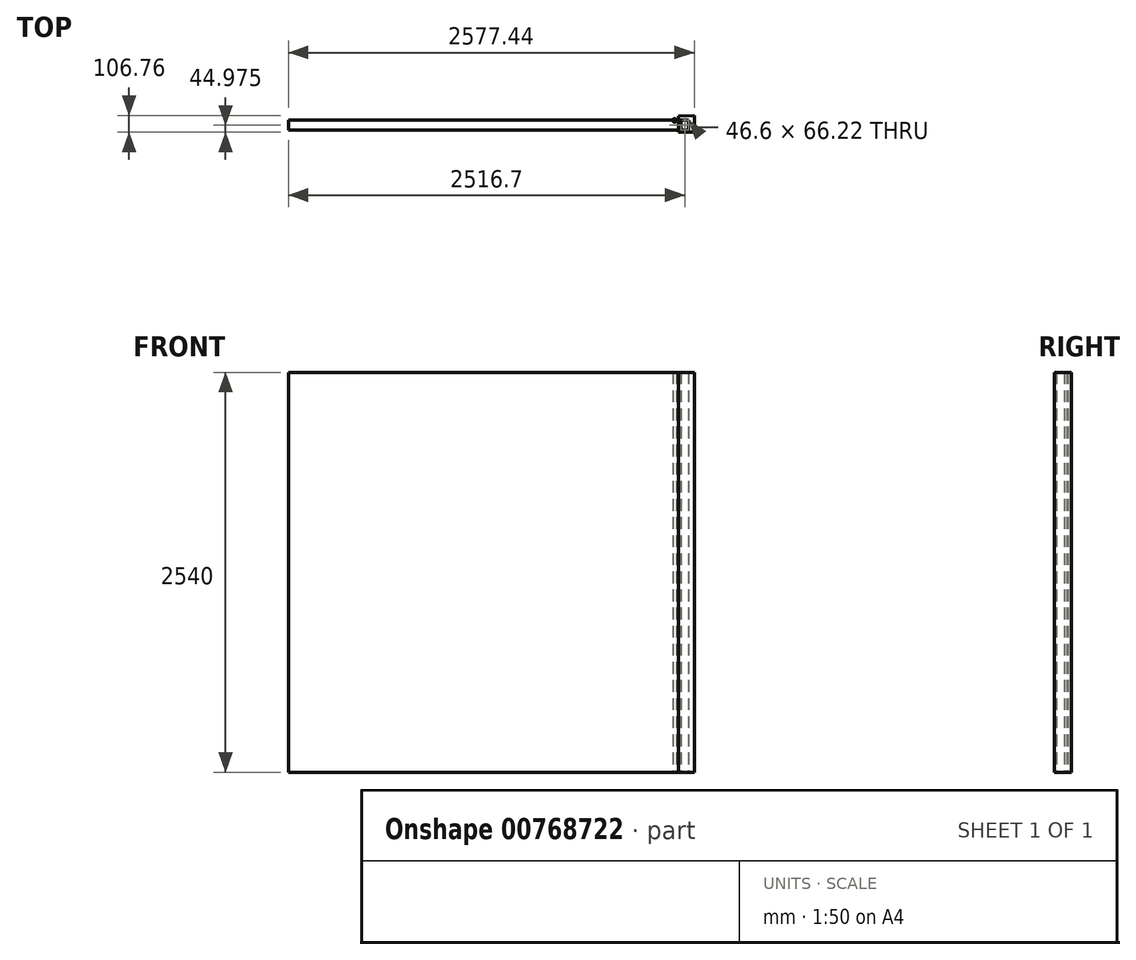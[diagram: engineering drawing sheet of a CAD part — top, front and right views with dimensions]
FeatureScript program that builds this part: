
annotation { "Feature Type Name" : "Feature", "Feature Type Description" : "" }
export const myFeature = defineFeature(function(context is Context, id is Id, definition is map)
    precondition{}
    {
        {
            var Q0;
            Q0=qCreatedBy(makeId("Top.planeOp"),FACE);
            var sketch = newSketch(context, id + "F0", { "sketchPlane" : qUnion([Q0])});
            skLineSegment(sketch, "E0", {"start": v(-32.23, 55.08) * mm, "end": v(-32.23, -47.42) * mm});
            skLineSegment(sketch, "E1", {"start": v(-32.23, -47.42) * mm, "end": v(67.44, -47.42) * mm});
            skLineSegment(sketch, "E2", {"start": v(67.44, -47.42) * mm, "end": v(67.44, 59.34) * mm});
            skLineSegment(sketch, "E3", {"start": v(67.44, 59.34) * mm, "end": v(-32.23, 55.08) * mm});
            skCircle(sketch, "E4", {"center": v(-58.35, 27.54) * mm, "radius": 10.88 * mm});
            skLineSegment(sketch, "E5.bottom", {"start": v(30, -35.56) * mm, "end": v(-16.6, -35.56) * mm});
            skLineSegment(sketch, "E5.top", {"start": v(30, 30.67) * mm, "end": v(-16.6, 30.67) * mm});
            skLineSegment(sketch, "E5.left", {"start": v(30, -35.56) * mm, "end": v(30, 30.67) * mm});
            skLineSegment(sketch, "E5.right", {"start": v(-16.6, -35.56) * mm, "end": v(-16.6, 30.67) * mm});
            skSolve(sketch);
        }
        {
            var Q0;
            Q0=makeQuery(id+"F0.imprint","IMPRINT",FACE,{"disambiguationData":[TD([[makeQuery(id+"F0.imprint","IMPRINT",EDGE,{"derivedFrom":sQuery(id+"F0.wireOp",EDGE,"E0")}),1.0]])]});
            var Q1;
            Q1=makeQuery(id+"F0.imprint","IMPRINT",FACE,{"disambiguationData":[TD([[makeQuery(id+"F0.imprint","IMPRINT",EDGE,{"derivedFrom":sQuery(id+"F0.wireOp",EDGE,"E4")}),1.0]])]});
            extrude(context, id + "F1", {"entities" : qUnion([Q0, Q1]), "depth" : 2540 * mm, "offsetDistance" : 25.4 * mm});
        }
        {
            var Q0;
            Q0=makeQuery(id+"F1.opExtrude","SWEPT_FACE",FACE,{"disambiguationData":[OSD([sQuery(id+"F0.wireOp",EDGE,"E5.left")])]});
            extrude(context, id + "F2", {"entities" : qUnion([Q0]), "depth" : 2540 * mm, "offsetDistance" : 25.4 * mm});
        }
    });
